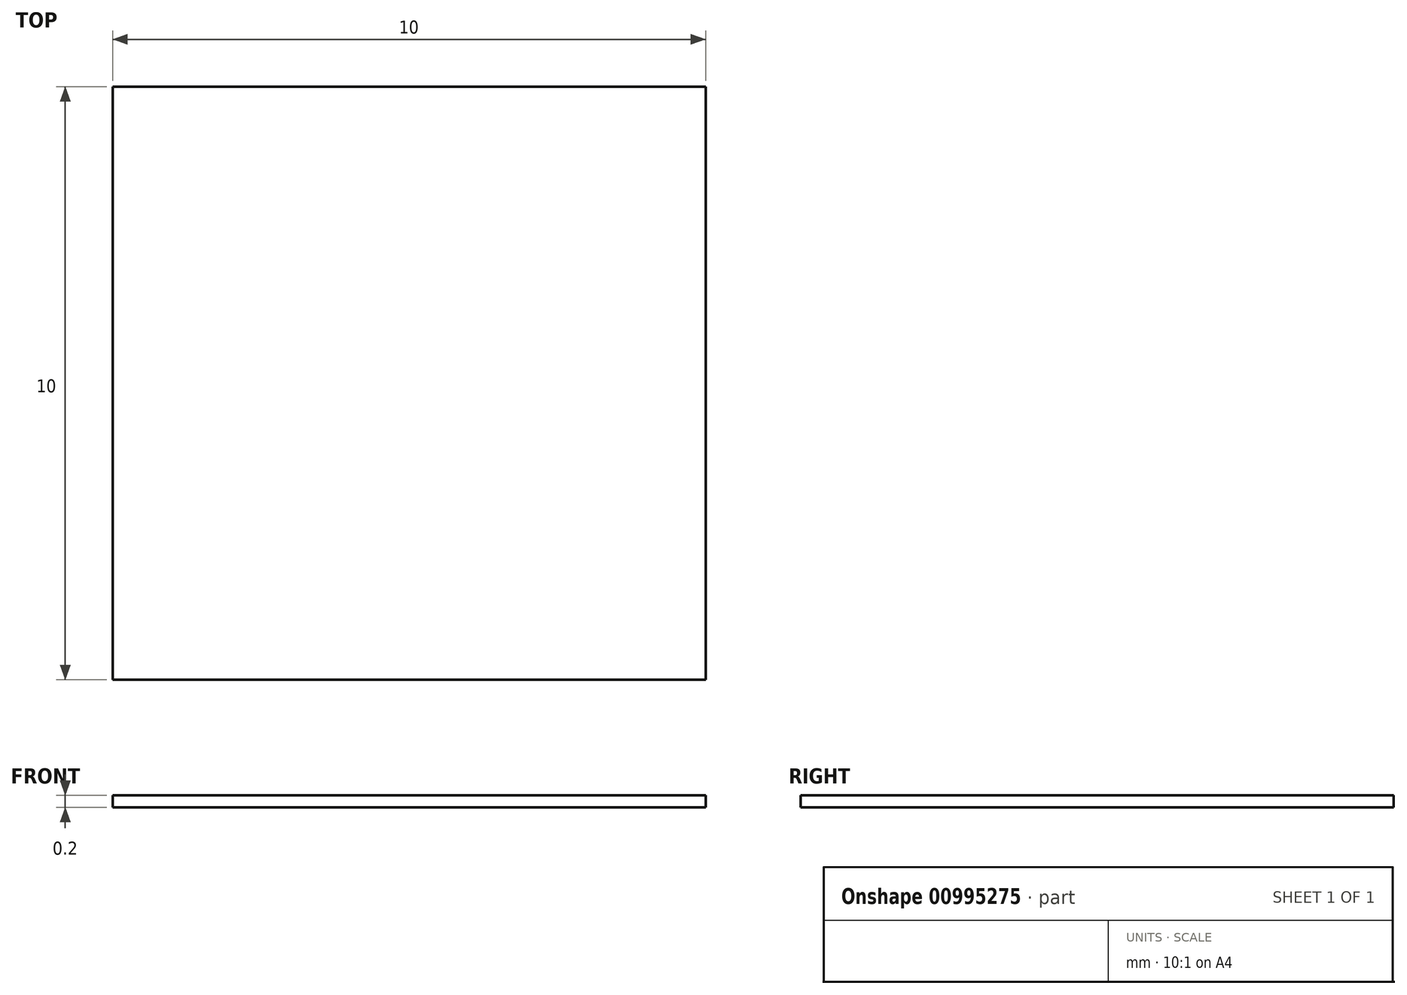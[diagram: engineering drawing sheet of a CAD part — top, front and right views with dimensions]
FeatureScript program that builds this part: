
annotation { "Feature Type Name" : "Feature", "Feature Type Description" : "" }
export const myFeature = defineFeature(function(context is Context, id is Id, definition is map)
    precondition{}
    {
        {
            var Q0;
            Q0=qCreatedBy(makeId("Top.planeOp"),FACE);
            var sketch = newSketch(context, id + "F0", { "sketchPlane" : qUnion([Q0])});
            skLineSegment(sketch, "E0.bottom", {"start": v(5, -5) * mm, "end": v(-5, -5) * mm});
            skLineSegment(sketch, "E0.top", {"start": v(5, 5) * mm, "end": v(-5, 5) * mm});
            skLineSegment(sketch, "E0.left", {"start": v(5, -5) * mm, "end": v(5, 5) * mm});
            skLineSegment(sketch, "E0.right", {"start": v(-5, -5) * mm, "end": v(-5, 5) * mm});
            skPoint(sketch, "E0.middle", {"position": v(0, 0) * mm});
            skSolve(sketch);
        }
        {
            var Q0;
            Q0=makeQuery(id+"F0.imprint","IMPRINT",FACE,{"disambiguationData":[TD([[makeQuery(id+"F0.imprint","IMPRINT",EDGE,{"derivedFrom":sQuery(id+"F0.wireOp",EDGE,"E0.bottom")}),-1.0]])]});
            extrude(context, id + "F1", {"entities" : qUnion([Q0]), "depth" : 0.2 * mm, "offsetDistance" : 25 * mm});
        }
    });
